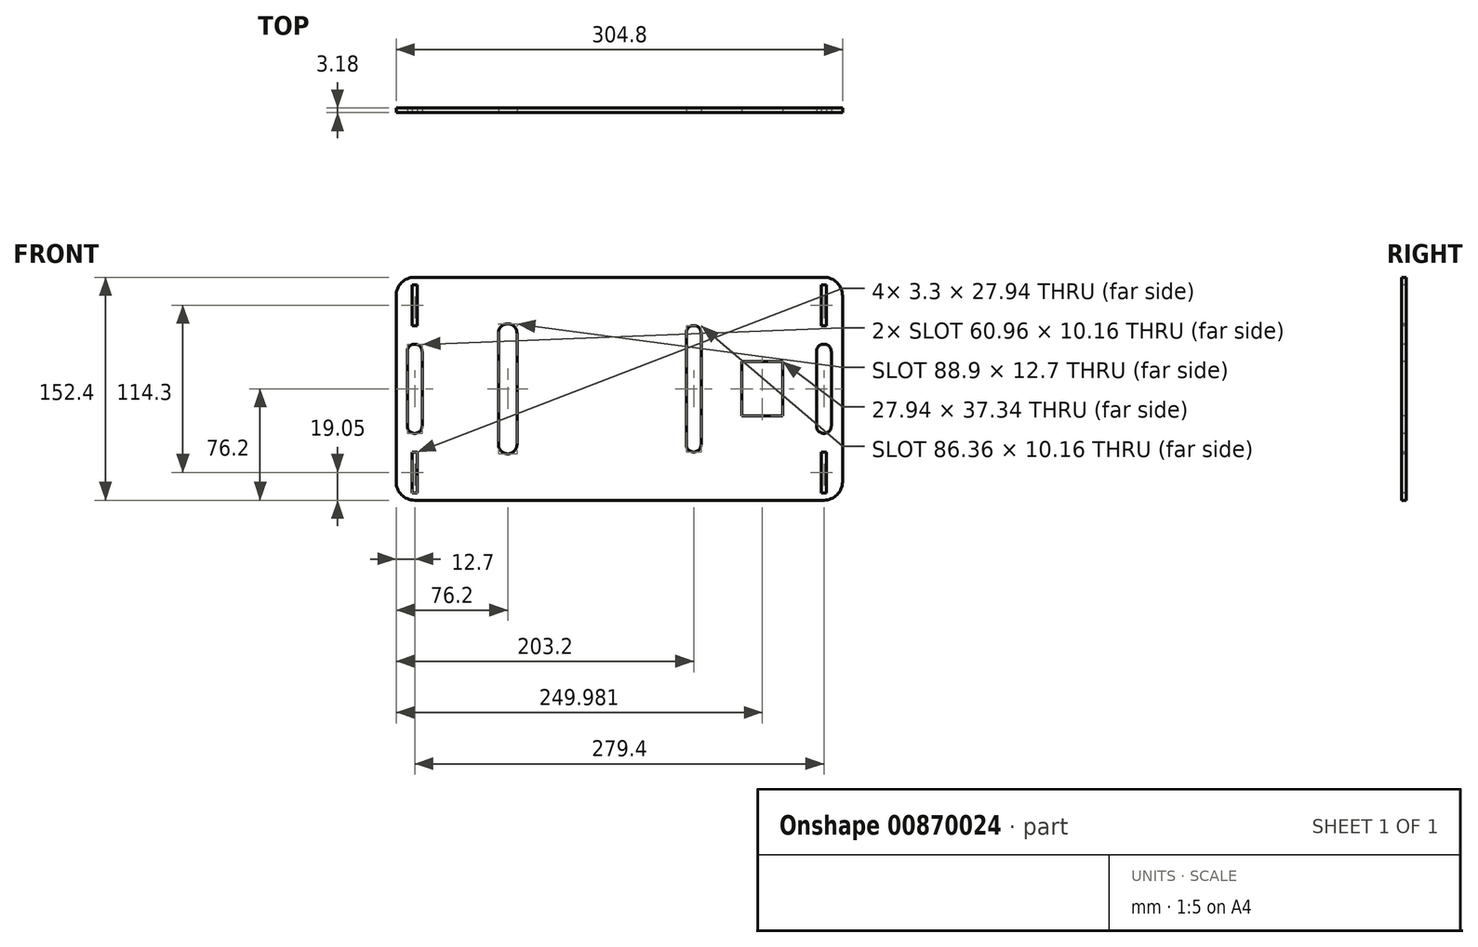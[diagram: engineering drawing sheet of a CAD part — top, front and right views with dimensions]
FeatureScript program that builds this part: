
annotation { "Feature Type Name" : "Feature", "Feature Type Description" : "" }
export const myFeature = defineFeature(function(context is Context, id is Id, definition is map)
    precondition{}
    {
        {
            var Q0;
            Q0=qCreatedBy(makeId("Front.planeOp"),FACE);
            var sketch = newSketch(context, id + "F0", { "sketchPlane" : qUnion([Q0])});
            skLineSegment(sketch, "E0.bottom", {"start": v(139.7, 76.2) * mm, "end": v(-139.7, 76.2) * mm});
            skLineSegment(sketch, "E0.top", {"start": v(139.7, -76.2) * mm, "end": v(-139.7, -76.2) * mm});
            skLineSegment(sketch, "E0.left", {"start": v(152.4, 63.5) * mm, "end": v(152.4, -63.5) * mm});
            skLineSegment(sketch, "E0.right", {"start": v(-152.4, 63.5) * mm, "end": v(-152.4, -63.5) * mm});
            skPoint(sketch, "E0.middle", {"position": v(0, 0) * mm});
            skPoint(sketch, "E1.visualSharp", {"position": v(-152.4, 76.2) * mm});
            skArc(sketch, "E1.filletArc", {"start": v(-139.7, 76.2) * mm, "mid": v(-148.68, 72.48) * mm, "end": v(-152.4, 63.5) * mm});
            skPoint(sketch, "E2.visualSharp", {"position": v(152.4, 76.2) * mm});
            skArc(sketch, "E2.filletArc", {"start": v(152.4, 63.5) * mm, "mid": v(148.68, 72.48) * mm, "end": v(139.7, 76.2) * mm});
            skPoint(sketch, "E3.visualSharp", {"position": v(152.4, -76.2) * mm});
            skArc(sketch, "E3.filletArc", {"start": v(139.7, -76.2) * mm, "mid": v(148.68, -72.48) * mm, "end": v(152.4, -63.5) * mm});
            skPoint(sketch, "E4.visualSharp", {"position": v(-152.4, -76.2) * mm});
            skArc(sketch, "E4.filletArc", {"start": v(-152.4, -63.5) * mm, "mid": v(-148.68, -72.48) * mm, "end": v(-139.7, -76.2) * mm});
            skSolve(sketch);
        }
        {
            var Q0;
            Q0=makeQuery(id+"F0.imprint","IMPRINT",FACE,{"disambiguationData":[TD([[makeQuery(id+"F0.imprint","IMPRINT",EDGE,{"derivedFrom":sQuery(id+"F0.wireOp",EDGE,"E0.bottom")}),1.0]])]});
            extrude(context, id + "F1", {"entities" : qUnion([Q0]), "depth" : 3.17 * mm, "offsetDistance" : 25.4 * mm});
        }
        {
            var Q0;
            Q0=makeQuery(id+"F1.opExtrude","CAP_FACE",FACE,{"disambiguationData":[OSD([sQuery(id+"F0.wireOp",EDGE,"E0.bottom"),sQuery(id+"F0.wireOp",EDGE,"E0.top"),sQuery(id+"F0.wireOp",EDGE,"E0.left"),sQuery(id+"F0.wireOp",EDGE,"E0.right"),sQuery(id+"F0.wireOp",EDGE,"E1.filletArc"),sQuery(id+"F0.wireOp",EDGE,"E2.filletArc"),sQuery(id+"F0.wireOp",EDGE,"E3.filletArc"),sQuery(id+"F0.wireOp",EDGE,"E4.filletArc")])],"isStart":false});
            var sketch = newSketch(context, id + "F2", { "sketchPlane" : qUnion([Q0])});
            skLineSegment(sketch, "E5", {"start": v(-76.2, 0) * mm, "end": v(-139.7, 0) * mm, "construction": true});
            skPoint(sketch, "E5.endSnap0", {"position": v(-152.4, 0) * mm});
            skLineSegment(sketch, "E6", {"start": v(-139.7, 0) * mm, "end": v(-139.7, 25.4) * mm});
            skLineSegment(sketch, "E7.MirrorCS", {"start": v(-139.7, 0) * mm, "end": v(-139.7, -25.4) * mm});
            skLineSegment(sketch, "E8", {"start": v(-76.2, 0) * mm, "end": v(-76.2, 38.1) * mm});
            skLineSegment(sketch, "E9", {"start": v(50.8, 0) * mm, "end": v(50.8, 38.1) * mm});
            skLineSegment(sketch, "E10.MirrorCS", {"start": v(50.8, 0) * mm, "end": v(50.8, -38.1) * mm});
            skArc(sketch, "E11.0.endCap", {"start": v(-134.62, -25.4) * mm, "mid": v(-139.7, -30.48) * mm, "end": v(-144.78, -25.4) * mm});
            skLineSegment(sketch, "E11.0.left", {"start": v(-134.62, 0) * mm, "end": v(-134.62, -25.4) * mm});
            skLineSegment(sketch, "E11.0.right", {"start": v(-144.78, 0) * mm, "end": v(-144.78, -25.4) * mm});
            skArc(sketch, "E11.1.endCap", {"start": v(-144.78, 25.4) * mm, "mid": v(-139.7, 30.48) * mm, "end": v(-134.62, 25.4) * mm});
            skLineSegment(sketch, "E11.1.left", {"start": v(-144.78, 0) * mm, "end": v(-144.78, 25.4) * mm});
            skLineSegment(sketch, "E11.1.right", {"start": v(-134.62, 0) * mm, "end": v(-134.62, 25.4) * mm});
            skArc(sketch, "E11.6.endCap", {"start": v(45.72, 38.1) * mm, "mid": v(50.8, 43.18) * mm, "end": v(55.88, 38.1) * mm});
            skLineSegment(sketch, "E11.6.left", {"start": v(45.72, 0) * mm, "end": v(45.72, 38.1) * mm});
            skLineSegment(sketch, "E11.6.right", {"start": v(55.88, 0) * mm, "end": v(55.88, 38.1) * mm});
            skArc(sketch, "E11.7.endCap", {"start": v(55.88, -38.1) * mm, "mid": v(50.8, -43.18) * mm, "end": v(45.72, -38.1) * mm});
            skLineSegment(sketch, "E11.7.left", {"start": v(55.88, 0) * mm, "end": v(55.88, -38.1) * mm});
            skLineSegment(sketch, "E11.7.right", {"start": v(45.72, 0) * mm, "end": v(45.72, -38.1) * mm});
            skLineSegment(sketch, "E12.bottom", {"start": v(111.55, 18.67) * mm, "end": v(83.61, 18.67) * mm});
            skLineSegment(sketch, "E12.top", {"start": v(111.55, -18.67) * mm, "end": v(83.61, -18.67) * mm});
            skLineSegment(sketch, "E12.left", {"start": v(111.55, 18.67) * mm, "end": v(111.55, -18.67) * mm});
            skLineSegment(sketch, "E12.right", {"start": v(83.61, 18.67) * mm, "end": v(83.61, -18.67) * mm});
            skPoint(sketch, "E12.middle", {"position": v(97.58, 0) * mm});
            skLineSegment(sketch, "E13", {"start": v(-139.7, 76.2) * mm, "end": v(-139.7, 57.15) * mm, "construction": true});
            skLineSegment(sketch, "E14.bottom", {"start": v(-138.05, 71.12) * mm, "end": v(-141.35, 71.12) * mm});
            skLineSegment(sketch, "E14.top", {"start": v(-138.05, 43.18) * mm, "end": v(-141.35, 43.18) * mm});
            skLineSegment(sketch, "E14.left", {"start": v(-138.05, 71.12) * mm, "end": v(-138.05, 43.18) * mm});
            skLineSegment(sketch, "E14.right", {"start": v(-141.35, 71.12) * mm, "end": v(-141.35, 43.18) * mm});
            skPoint(sketch, "E14.middle", {"position": v(-139.7, 57.15) * mm});
            skLineSegment(sketch, "E15.MirrorCS", {"start": v(-138.05, -71.12) * mm, "end": v(-141.35, -71.12) * mm});
            skPoint(sketch, "E16.MirrorP", {"position": v(-139.7, -57.15) * mm});
            skLineSegment(sketch, "E17.MirrorCS", {"start": v(-141.35, -71.12) * mm, "end": v(-141.35, -43.18) * mm});
            skLineSegment(sketch, "E18.MirrorCS", {"start": v(-138.05, -71.12) * mm, "end": v(-138.05, -43.18) * mm});
            skLineSegment(sketch, "E19.MirrorCS", {"start": v(-138.05, -43.18) * mm, "end": v(-141.35, -43.18) * mm});
            skLineSegment(sketch, "E20.MirrorCS", {"start": v(141.35, 71.12) * mm, "end": v(141.35, 43.18) * mm});
            skLineSegment(sketch, "E21.MirrorCS", {"start": v(138.05, 71.12) * mm, "end": v(138.05, 43.18) * mm});
            skLineSegment(sketch, "E22.MirrorCS", {"start": v(138.05, 71.12) * mm, "end": v(141.35, 71.12) * mm});
            skPoint(sketch, "E23.MirrorP", {"position": v(139.7, 57.15) * mm});
            skLineSegment(sketch, "E24.MirrorCS", {"start": v(138.05, 43.18) * mm, "end": v(141.35, 43.18) * mm});
            skLineSegment(sketch, "E25.MirrorCS", {"start": v(139.7, 76.2) * mm, "end": v(139.7, 57.15) * mm, "construction": true});
            skPoint(sketch, "E26.MirrorP", {"position": v(139.7, -57.15) * mm});
            skLineSegment(sketch, "E27.MirrorCS", {"start": v(141.35, -71.12) * mm, "end": v(141.35, -43.18) * mm});
            skLineSegment(sketch, "E28.MirrorCS", {"start": v(138.05, -71.12) * mm, "end": v(141.35, -71.12) * mm});
            skLineSegment(sketch, "E29.MirrorCS", {"start": v(138.05, -43.18) * mm, "end": v(141.35, -43.18) * mm});
            skLineSegment(sketch, "E30.MirrorCS", {"start": v(138.05, -71.12) * mm, "end": v(138.05, -43.18) * mm});
            skLineSegment(sketch, "E31.MirrorCS", {"start": v(134.62, 0) * mm, "end": v(134.62, -25.4) * mm});
            skLineSegment(sketch, "E32.MirrorCS", {"start": v(144.78, 0) * mm, "end": v(144.78, 25.4) * mm});
            skLineSegment(sketch, "E33.MirrorCS", {"start": v(76.2, 0) * mm, "end": v(139.7, 0) * mm, "construction": true});
            skLineSegment(sketch, "E34.MirrorCS", {"start": v(134.62, 0) * mm, "end": v(134.62, 25.4) * mm});
            skLineSegment(sketch, "E35.MirrorCS", {"start": v(139.7, 0) * mm, "end": v(139.7, 25.4) * mm});
            skArc(sketch, "E36.MirrorCS", {"start": v(144.78, 25.4) * mm, "mid": v(139.7, 30.48) * mm, "end": v(134.62, 25.4) * mm});
            skLineSegment(sketch, "E37.MirrorCS", {"start": v(144.78, 0) * mm, "end": v(144.78, -25.4) * mm});
            skLineSegment(sketch, "E38.MirrorCS", {"start": v(139.7, 0) * mm, "end": v(139.7, -25.4) * mm});
            skArc(sketch, "E39.MirrorCS", {"start": v(134.62, -25.4) * mm, "mid": v(139.7, -30.48) * mm, "end": v(144.78, -25.4) * mm});
            skLineSegment(sketch, "E40", {"start": v(-76.2, 0) * mm, "end": v(-76.2, -38.1) * mm});
            skArc(sketch, "E41.0.endCap", {"start": v(-82.55, 38.1) * mm, "mid": v(-76.2, 44.45) * mm, "end": v(-69.85, 38.1) * mm});
            skLineSegment(sketch, "E41.0.left", {"start": v(-82.55, 0) * mm, "end": v(-82.55, 38.1) * mm});
            skLineSegment(sketch, "E41.0.right", {"start": v(-69.85, 0) * mm, "end": v(-69.85, 38.1) * mm});
            skArc(sketch, "E41.1.endCap", {"start": v(-69.85, -38.1) * mm, "mid": v(-76.2, -44.45) * mm, "end": v(-82.55, -38.1) * mm});
            skLineSegment(sketch, "E41.1.left", {"start": v(-69.85, 0) * mm, "end": v(-69.85, -38.1) * mm});
            skLineSegment(sketch, "E41.1.right", {"start": v(-82.55, 0) * mm, "end": v(-82.55, -38.1) * mm});
            skSolve(sketch);
        }
        {
            var Q0;
            Q0 = qSketchRegion(id + "F2", true);
            extrude(context, id + "F3", {"entities" : qUnion([Q0]), "operationType" : NewBodyOperationType.REMOVE, "oppositeDirection" : true, "depth" : 25.4 * mm, "offsetDistance" : 25.4 * mm});
        }
        {
            var Q0;
            Q0=makeQuery(id+"F1.opExtrude","SWEPT_BODY",BODY,{"disambiguationData":[OSD([sQuery(id+"F0.wireOp",EDGE,"E0.bottom"),sQuery(id+"F0.wireOp",EDGE,"E0.top"),sQuery(id+"F0.wireOp",EDGE,"E0.left"),sQuery(id+"F0.wireOp",EDGE,"E0.right"),sQuery(id+"F0.wireOp",EDGE,"E1.filletArc"),sQuery(id+"F0.wireOp",EDGE,"E2.filletArc"),sQuery(id+"F0.wireOp",EDGE,"E3.filletArc"),sQuery(id+"F0.wireOp",EDGE,"E4.filletArc")])]});
            transform(context, id + "F4", {"entities" : qUnion([Q0]), "transformType" : TransformType.TRANSLATION_3D, "dx" : 0 * mm, "dy" : 0 * mm, "dz" : 0 * mm, "makeCopy" : true});
        }
        {
            var Q0;
            Q0=makeQuery(id+"F4.opPattern","COPY",BODY,{"derivedFrom":makeQuery(id+"F1.opExtrude","SWEPT_BODY",BODY,{"disambiguationData":[OSD([sQuery(id+"F0.wireOp",EDGE,"E0.bottom"),sQuery(id+"F0.wireOp",EDGE,"E0.top"),sQuery(id+"F0.wireOp",EDGE,"E0.left"),sQuery(id+"F0.wireOp",EDGE,"E0.right"),sQuery(id+"F0.wireOp",EDGE,"E1.filletArc"),sQuery(id+"F0.wireOp",EDGE,"E2.filletArc"),sQuery(id+"F0.wireOp",EDGE,"E3.filletArc"),sQuery(id+"F0.wireOp",EDGE,"E4.filletArc")])]}),"instanceName":"1"});
            deleteBodies(context, id + "F5", {"entities" : qUnion([Q0])});
        }
    });
